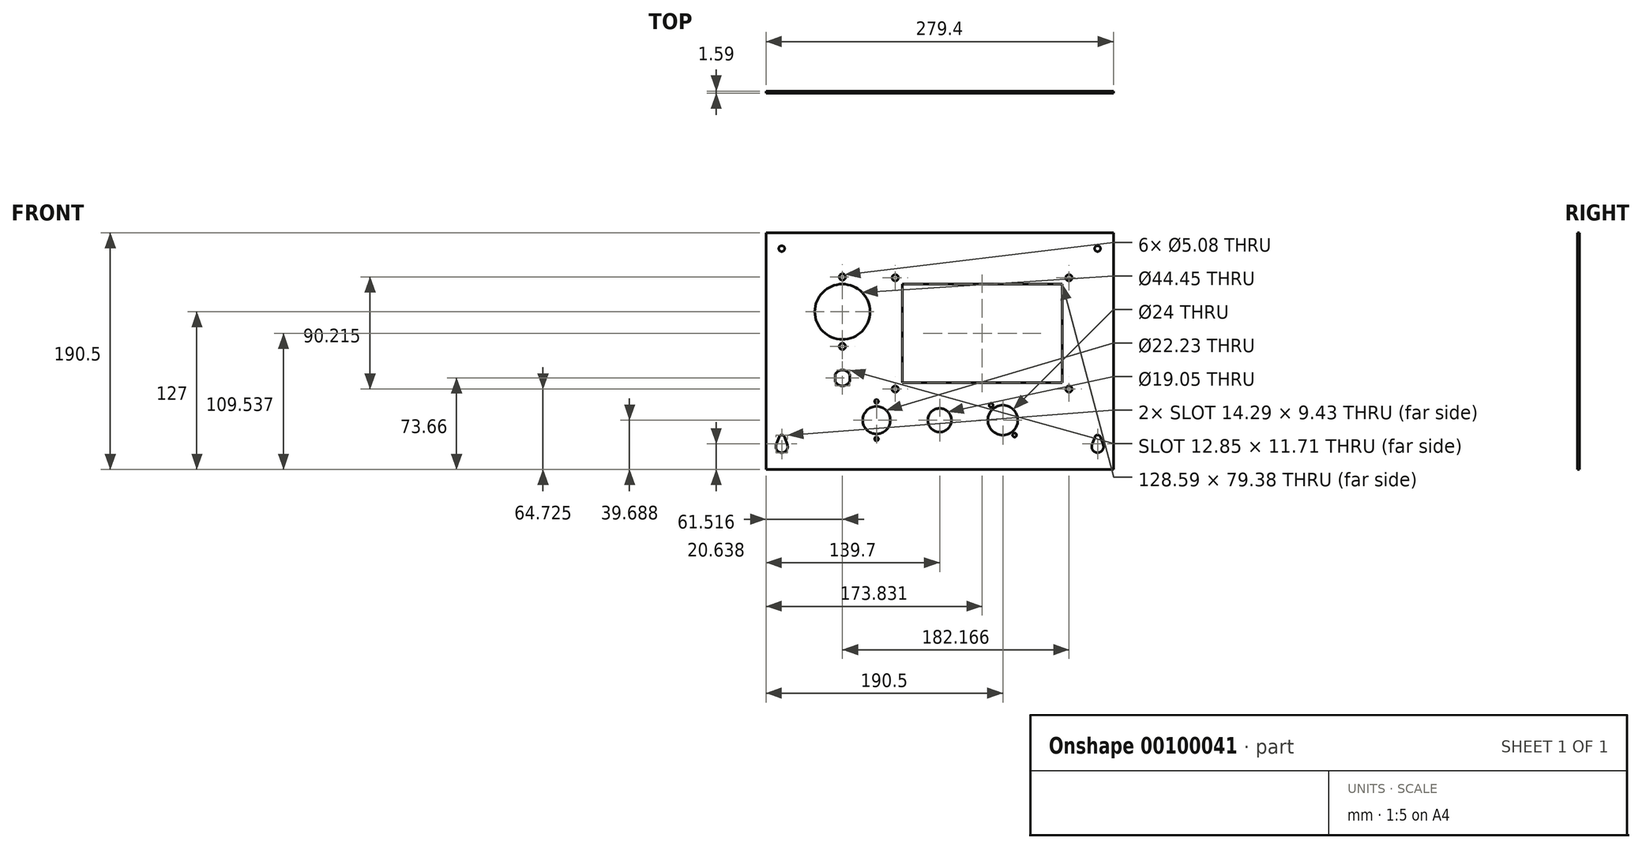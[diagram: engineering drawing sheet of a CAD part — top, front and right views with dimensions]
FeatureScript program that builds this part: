
annotation { "Feature Type Name" : "Feature", "Feature Type Description" : "" }
export const myFeature = defineFeature(function(context is Context, id is Id, definition is map)
    precondition{}
    {
        {
            var Q0;
            Q0=qCreatedBy(makeId("Front.planeOp"),FACE);
            var sketch = newSketch(context, id + "F0", { "sketchPlane" : qUnion([Q0])});
            skLineSegment(sketch, "E0.bottom", {"start": v(139.7, 95.25) * mm, "end": v(-139.7, 95.25) * mm});
            skLineSegment(sketch, "E0.top", {"start": v(139.7, -95.25) * mm, "end": v(-139.7, -95.25) * mm});
            skLineSegment(sketch, "E0.left", {"start": v(139.7, 95.25) * mm, "end": v(139.7, -95.25) * mm});
            skLineSegment(sketch, "E0.right", {"start": v(-139.7, 95.25) * mm, "end": v(-139.7, -95.25) * mm});
            skPoint(sketch, "E0.middle", {"position": v(0, 0) * mm});
            skSolve(sketch);
        }
        {
            var Q0;
            Q0=makeQuery(id+"F0.imprint","IMPRINT",FACE,{"disambiguationData":[TD([[makeQuery(id+"F0.imprint","IMPRINT",EDGE,{"derivedFrom":sQuery(id+"F0.wireOp",EDGE,"E0.bottom")}),1.0]])]});
            extrude(context, id + "F1", {"entities" : qUnion([Q0]), "depth" : 1.59 * mm});
        }
        {
            var Q0;
            Q0=makeQuery(id+"F1.opExtrude","CAP_FACE",FACE,{"disambiguationData":[OSD([sQuery(id+"F0.wireOp",EDGE,"E0.bottom"),sQuery(id+"F0.wireOp",EDGE,"E0.top"),sQuery(id+"F0.wireOp",EDGE,"E0.left"),sQuery(id+"F0.wireOp",EDGE,"E0.right")])],"isStart":false});
            var sketch = newSketch(context, id + "F2", { "sketchPlane" : qUnion([Q0])});
            skLineSegment(sketch, "E1.0", {"start": v(139.7, 95.25) * mm, "end": v(-139.7, 95.25) * mm, "construction": true});
            skLineSegment(sketch, "E1.1", {"start": v(-139.7, 95.25) * mm, "end": v(-139.7, -95.25) * mm, "construction": true});
            skLineSegment(sketch, "E1.2", {"start": v(139.7, 95.25) * mm, "end": v(139.7, -95.25) * mm, "construction": true});
            skLineSegment(sketch, "E2.0", {"start": v(-114.3, 69.85) * mm, "end": v(-114.3, -95.25) * mm, "construction": true});
            skLineSegment(sketch, "E2.1", {"start": v(139.7, 69.85) * mm, "end": v(-139.7, 69.85) * mm, "construction": true});
            skLineSegment(sketch, "E2.2", {"start": v(114.3, 69.85) * mm, "end": v(114.3, -95.25) * mm, "construction": true});
            skLineSegment(sketch, "E3.bottom", {"start": v(98.43, 53.98) * mm, "end": v(-30.16, 53.98) * mm});
            skLineSegment(sketch, "E3.top", {"start": v(98.43, -25.4) * mm, "end": v(-30.16, -25.4) * mm});
            skLineSegment(sketch, "E3.left", {"start": v(98.43, 53.98) * mm, "end": v(98.43, -25.4) * mm});
            skLineSegment(sketch, "E3.right", {"start": v(-30.16, 53.98) * mm, "end": v(-30.16, -25.4) * mm});
            skLineSegment(sketch, "E4", {"start": v(98.43, 14.29) * mm, "end": v(114.3, 14.29) * mm, "construction": true});
            skLineSegment(sketch, "E5", {"start": v(34.13, 53.98) * mm, "end": v(34.13, 69.85) * mm, "construction": true});
            skLineSegment(sketch, "E6.bottom", {"start": v(-35.72, -30.52) * mm, "end": v(103.98, -30.52) * mm, "construction": true});
            skLineSegment(sketch, "E6.top", {"start": v(-35.72, 59.1) * mm, "end": v(103.98, 59.1) * mm, "construction": true});
            skLineSegment(sketch, "E6.left", {"start": v(-35.72, -30.52) * mm, "end": v(-35.72, 59.1) * mm, "construction": true});
            skLineSegment(sketch, "E6.right", {"start": v(103.98, -30.52) * mm, "end": v(103.98, 59.1) * mm, "construction": true});
            skLineSegment(sketch, "E7", {"start": v(-30.16, 14.29) * mm, "end": v(-35.72, 14.29) * mm, "construction": true});
            skLineSegment(sketch, "E8", {"start": v(103.98, 14.29) * mm, "end": v(98.43, 14.29) * mm, "construction": true});
            skLineSegment(sketch, "E9", {"start": v(34.13, 59.1) * mm, "end": v(34.13, 53.98) * mm, "construction": true});
            skLineSegment(sketch, "E10", {"start": v(34.13, -25.4) * mm, "end": v(34.13, -30.52) * mm, "construction": true});
            skCircle(sketch, "E11", {"center": v(-35.72, 59.1) * mm, "radius": 2.54 * mm});
            skCircle(sketch, "E12", {"center": v(103.98, 59.1) * mm, "radius": 2.54 * mm});
            skCircle(sketch, "E13", {"center": v(103.98, -30.52) * mm, "radius": 2.54 * mm});
            skCircle(sketch, "E14", {"center": v(-35.72, -30.52) * mm, "radius": 2.54 * mm});
            skLineSegment(sketch, "E15.bottom", {"start": v(110.33, 65.09) * mm, "end": v(-42.07, 65.09) * mm, "construction": true});
            skLineSegment(sketch, "E15.top", {"start": v(110.33, -36.51) * mm, "end": v(-42.07, -36.51) * mm, "construction": true});
            skLineSegment(sketch, "E15.left", {"start": v(110.33, 65.09) * mm, "end": v(110.33, -36.51) * mm, "construction": true});
            skLineSegment(sketch, "E15.right", {"start": v(-42.07, 65.09) * mm, "end": v(-42.07, -36.51) * mm, "construction": true});
            skLineSegment(sketch, "E16", {"start": v(-30.16, 53.98) * mm, "end": v(-42.07, 65.09) * mm, "construction": true});
            skLineSegment(sketch, "E17", {"start": v(-30.16, -25.4) * mm, "end": v(-42.07, -36.51) * mm, "construction": true});
            skLineSegment(sketch, "E18", {"start": v(98.43, -25.4) * mm, "end": v(110.33, -36.51) * mm, "construction": true});
            skLineSegment(sketch, "E19", {"start": v(98.43, 53.98) * mm, "end": v(110.33, 65.09) * mm, "construction": true});
            skLineSegment(sketch, "E20", {"start": v(-114.3, -69.85) * mm, "end": v(-82.55, -69.85) * mm, "construction": true});
            skLineSegment(sketch, "E21", {"start": v(-82.55, -69.85) * mm, "end": v(-82.55, -95.25) * mm, "construction": true});
            skLineSegment(sketch, "E22", {"start": v(82.55, -69.85) * mm, "end": v(82.55, -95.25) * mm, "construction": true});
            skLineSegment(sketch, "E23.trimOffspring", {"start": v(82.55, -69.85) * mm, "end": v(114.3, -69.85) * mm, "construction": true});
            skSolve(sketch);
        }
        {
            var Q0;
            Q0 = qSketchRegion(id + "F2", true);
            extrude(context, id + "F3", {"entities" : qUnion([Q0]), "operationType" : NewBodyOperationType.REMOVE, "oppositeDirection" : true, "depth" : 25.4 * mm});
        }
        {
            var Q0;
            Q0=makeQuery(id+"F1.opExtrude","CAP_FACE",FACE,{"disambiguationData":[OSD([sQuery(id+"F0.wireOp",EDGE,"E0.bottom"),sQuery(id+"F0.wireOp",EDGE,"E0.top"),sQuery(id+"F0.wireOp",EDGE,"E0.left"),sQuery(id+"F0.wireOp",EDGE,"E0.right")])],"isStart":false});
            var sketch = newSketch(context, id + "F4", { "sketchPlane" : qUnion([Q0])});
            skCircle(sketch, "E24", {"center": v(-78.18, 31.75) * mm, "radius": 22.23 * mm});
            skCircle(sketch, "E25", {"center": v(-78.18, 59.7) * mm, "radius": 2.54 * mm});
            skCircle(sketch, "E26", {"center": v(-78.18, 3.81) * mm, "radius": 2.54 * mm});
            skLineSegment(sketch, "E27", {"start": v(-78.18, 59.7) * mm, "end": v(-78.18, 31.75) * mm, "construction": true});
            skLineSegment(sketch, "E28", {"start": v(-78.18, 31.75) * mm, "end": v(-78.18, 3.81) * mm, "construction": true});
            skCircle(sketch, "E29", {"center": v(-78.18, 31.75) * mm, "radius": 33.02 * mm, "construction": true});
            skLineSegment(sketch, "E30.0", {"start": v(-42.07, 65.09) * mm, "end": v(-42.07, -36.51) * mm, "construction": true});
            skLineSegment(sketch, "E30.1", {"start": v(-114.3, 69.85) * mm, "end": v(-114.3, -95.25) * mm, "construction": true});
            skLineSegment(sketch, "E31", {"start": v(-78.18, 31.75) * mm, "end": v(-114.3, 31.75) * mm, "construction": true});
            skLineSegment(sketch, "E32", {"start": v(-78.18, 31.75) * mm, "end": v(-42.07, 31.75) * mm, "construction": true});
            skSolve(sketch);
        }
        {
            var Q0;
            Q0 = qSketchRegion(id + "F4", true);
            extrude(context, id + "F5", {"entities" : qUnion([Q0]), "operationType" : NewBodyOperationType.REMOVE, "oppositeDirection" : true, "depth" : 25.4 * mm});
        }
        {
            var Q0;
            Q0=makeQuery(id+"F1.opExtrude","CAP_FACE",FACE,{"disambiguationData":[OSD([sQuery(id+"F0.wireOp",EDGE,"E0.bottom"),sQuery(id+"F0.wireOp",EDGE,"E0.top"),sQuery(id+"F0.wireOp",EDGE,"E0.left"),sQuery(id+"F0.wireOp",EDGE,"E0.right")])],"isStart":false});
            var sketch = newSketch(context, id + "F6", { "sketchPlane" : qUnion([Q0])});
            skCircle(sketch, "E33", {"center": v(50.8, -55.56) * mm, "radius": 12 * mm});
            skCircle(sketch, "E34", {"center": v(41.34, -43.56) * mm, "radius": 1.59 * mm});
            skCircle(sketch, "E35", {"center": v(60.26, -67.56) * mm, "radius": 1.59 * mm});
            skLineSegment(sketch, "E36", {"start": v(41.34, -43.56) * mm, "end": v(50.8, -55.56) * mm, "construction": true});
            skLineSegment(sketch, "E37", {"start": v(50.8, -55.56) * mm, "end": v(60.26, -67.56) * mm, "construction": true});
            skCircle(sketch, "E38", {"center": v(0, -55.56) * mm, "radius": 9.53 * mm});
            skArc(sketch, "E39", {"start": v(-84.04, -24.24) * mm, "mid": v(-78.18, -28.02) * mm, "end": v(-72.33, -24.24) * mm});
            skLineSegment(sketch, "E40", {"start": v(-84.04, -18.94) * mm, "end": v(-84.04, -24.24) * mm});
            skLineSegment(sketch, "E41", {"start": v(-72.33, -24.24) * mm, "end": v(-72.33, -18.94) * mm});
            skLineSegment(sketch, "E42", {"start": v(-84.04, -21.59) * mm, "end": v(-78.18, -21.59) * mm, "construction": true});
            skLineSegment(sketch, "E43", {"start": v(-72.33, -21.59) * mm, "end": v(-78.18, -21.59) * mm, "construction": true});
            skArc(sketch, "E44.trimOffspring", {"start": v(-72.33, -18.94) * mm, "mid": v(-78.18, -15.16) * mm, "end": v(-84.04, -18.94) * mm});
            skCircle(sketch, "E45", {"center": v(-50.8, -55.56) * mm, "radius": 11.11 * mm});
            skLineSegment(sketch, "E46", {"start": v(-50.8, -55.56) * mm, "end": v(0, -55.56) * mm, "construction": true});
            skLineSegment(sketch, "E47", {"start": v(0, -55.56) * mm, "end": v(50.8, -55.56) * mm, "construction": true});
            skLineSegment(sketch, "E48", {"start": v(0, -55.56) * mm, "end": v(0, -95.25) * mm, "construction": true});
            skLineSegment(sketch, "E49.0", {"start": v(110.33, -36.51) * mm, "end": v(-42.07, -36.51) * mm, "construction": true});
            skLineSegment(sketch, "E50", {"start": v(0, -55.56) * mm, "end": v(0, -36.51) * mm, "construction": true});
            skCircle(sketch, "E51", {"center": v(-50.8, -40.48) * mm, "radius": 1.59 * mm});
            skCircle(sketch, "E52", {"center": v(-50.8, -70.64) * mm, "radius": 1.59 * mm});
            skLineSegment(sketch, "E53", {"start": v(-50.8, -40.48) * mm, "end": v(-50.8, -55.56) * mm, "construction": true});
            skLineSegment(sketch, "E54", {"start": v(-50.8, -55.56) * mm, "end": v(-50.8, -70.64) * mm, "construction": true});
            skSolve(sketch);
        }
        {
            var Q0;
            Q0 = qSketchRegion(id + "F6", true);
            extrude(context, id + "F7", {"entities" : qUnion([Q0]), "operationType" : NewBodyOperationType.REMOVE, "oppositeDirection" : true, "depth" : 25.4 * mm});
        }
        {
            var Q0;
            Q0=makeQuery(id+"F1.opExtrude","CAP_FACE",FACE,{"disambiguationData":[OSD([sQuery(id+"F0.wireOp",EDGE,"E0.bottom"),sQuery(id+"F0.wireOp",EDGE,"E0.top"),sQuery(id+"F0.wireOp",EDGE,"E0.left"),sQuery(id+"F0.wireOp",EDGE,"E0.right")])],"isStart":false});
            var sketch = newSketch(context, id + "F8", { "sketchPlane" : qUnion([Q0])});
            skCircle(sketch, "E55", {"center": v(-127, 82.55) * mm, "radius": 2.38 * mm});
            skCircle(sketch, "E56", {"center": v(127, 82.55) * mm, "radius": 2.38 * mm});
            skArc(sketch, "E57", {"start": v(-124.75, -69.06) * mm, "mid": v(-127, -67.47) * mm, "end": v(-129.25, -69.06) * mm});
            skArc(sketch, "E58", {"start": v(129.25, -69.06) * mm, "mid": v(127, -67.47) * mm, "end": v(124.75, -69.06) * mm});
            skArc(sketch, "E59", {"start": v(122.5, -75.4) * mm, "mid": v(127, -81.76) * mm, "end": v(131.5, -75.4) * mm});
            skLineSegment(sketch, "E60", {"start": v(124.75, -69.06) * mm, "end": v(122.5, -75.4) * mm});
            skLineSegment(sketch, "E61", {"start": v(129.25, -69.06) * mm, "end": v(131.5, -75.4) * mm});
            skArc(sketch, "E62", {"start": v(-131.5, -75.4) * mm, "mid": v(-127, -81.76) * mm, "end": v(-122.5, -75.4) * mm});
            skLineSegment(sketch, "E63", {"start": v(-129.25, -69.06) * mm, "end": v(-131.5, -75.4) * mm});
            skLineSegment(sketch, "E64", {"start": v(-124.75, -69.06) * mm, "end": v(-122.5, -75.4) * mm});
            skSolve(sketch);
        }
        {
            var Q0;
            Q0 = qSketchRegion(id + "F8", true);
            extrude(context, id + "F9", {"entities" : qUnion([Q0]), "operationType" : NewBodyOperationType.REMOVE, "oppositeDirection" : true, "depth" : 25.4 * mm});
        }
    });
